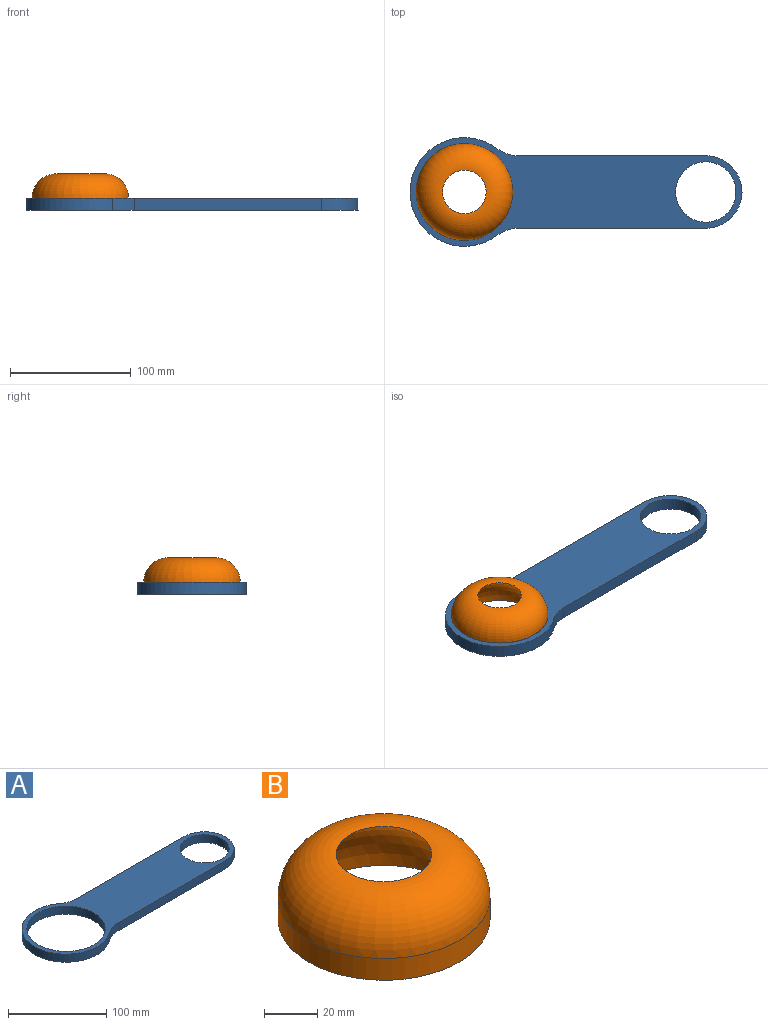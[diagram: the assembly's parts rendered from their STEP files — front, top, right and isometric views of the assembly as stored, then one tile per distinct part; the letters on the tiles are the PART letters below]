
ASSEMBLY  parts=2 mates=1
PART A: 10 faces, bbox 275x90x10 mm
  f0: plane 155x10mm, normal (0,1,0), area 1550mm2, adj f1,f6,f8,f9
  f1: cylinder r=30mm len=18mm, axis (0,0,-1), area 193.1mm2, adj f0,f2,f8,f9
  f2: cylinder r=45mm len=90mm, axis (0,0,-1), area 1992.9mm2, adj f1,f3,f8,f9
  f3: cylinder r=30mm len=18mm, axis (0,0,-1), area 193.1mm2, adj f2,f4,f8,f9
  f4: plane 155x10mm, normal (0,-1,0), area 1550mm2, adj f3,f6,f8,f9
  f5: cylinder r=40mm len=80mm, axis (0,0,-1), area 2513.3mm2, adj f8,f9
  f6: cylinder r=30mm len=60mm, axis (0,0,-1), area 942.5mm2, adj f0,f4,f8,f9
  f7: cylinder r=25mm len=50mm, axis (0,0,-1), area 1570.8mm2, adj f8,f9
  f8: plane 275x90mm, normal (0,0,1), area 10328.5mm2, adj f0,f1,f2,f3,f4,f5,f6,f7
  f9: plane 275x90mm, normal (0,0,-1), area 10328.5mm2, adj f0,f1,f2,f3,f4,f5,f6,f7
PART B: 4 faces, bbox 80x80x30.1 mm
  f0: cylinder r=40mm len=80mm, axis (0,0,-1), area 2513.3mm2, adj f1,f3
  f1: plane 80x80mm, normal (0,0,-1), area 1178.1mm2, adj f0,f2
  f2: sphere r=35mm, area 6597.3mm2, adj f1,f3
  f3: torus R=19.91mm, axis (0,0,-1), area 6708.2mm2, adj f0,f2
PLACE A t=(-64.51,13.01,-48.84)mm
PLACE B t=(-64.51,13.01,-48.84)mm
MATE revolute B.f0 <-> A.f5  axis (0,0,-1) through (-64.51,13.01,-43.84)mm
